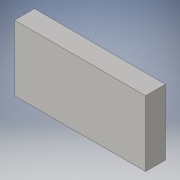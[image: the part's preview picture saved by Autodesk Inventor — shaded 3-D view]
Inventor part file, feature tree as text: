
AUTODESK INVENTOR PART (.ipt)
format: ipt  version: 2016 (Build 200138000, 138)  size: 82,944 bytes
history: native  units: in
note: dims shown in document units (in); Inventor stores cm internally (conversion verified against a paired STEP export)
features: extrude x1, sketch x1
ambient origin geometry x8: Origin, YZ Plane, XZ Plane, XY Plane, X Axis, Y Axis, Z Axis, Center Point
bodies: Solid1 (feature_tree)
feature tree (2):
  extrude  "Extrusion1"  Depth=29.5276in
  sketch  "Sketch1"  dims[d0=59.0551in d1=29.5276in d2=9.0in d3=0.0in]
